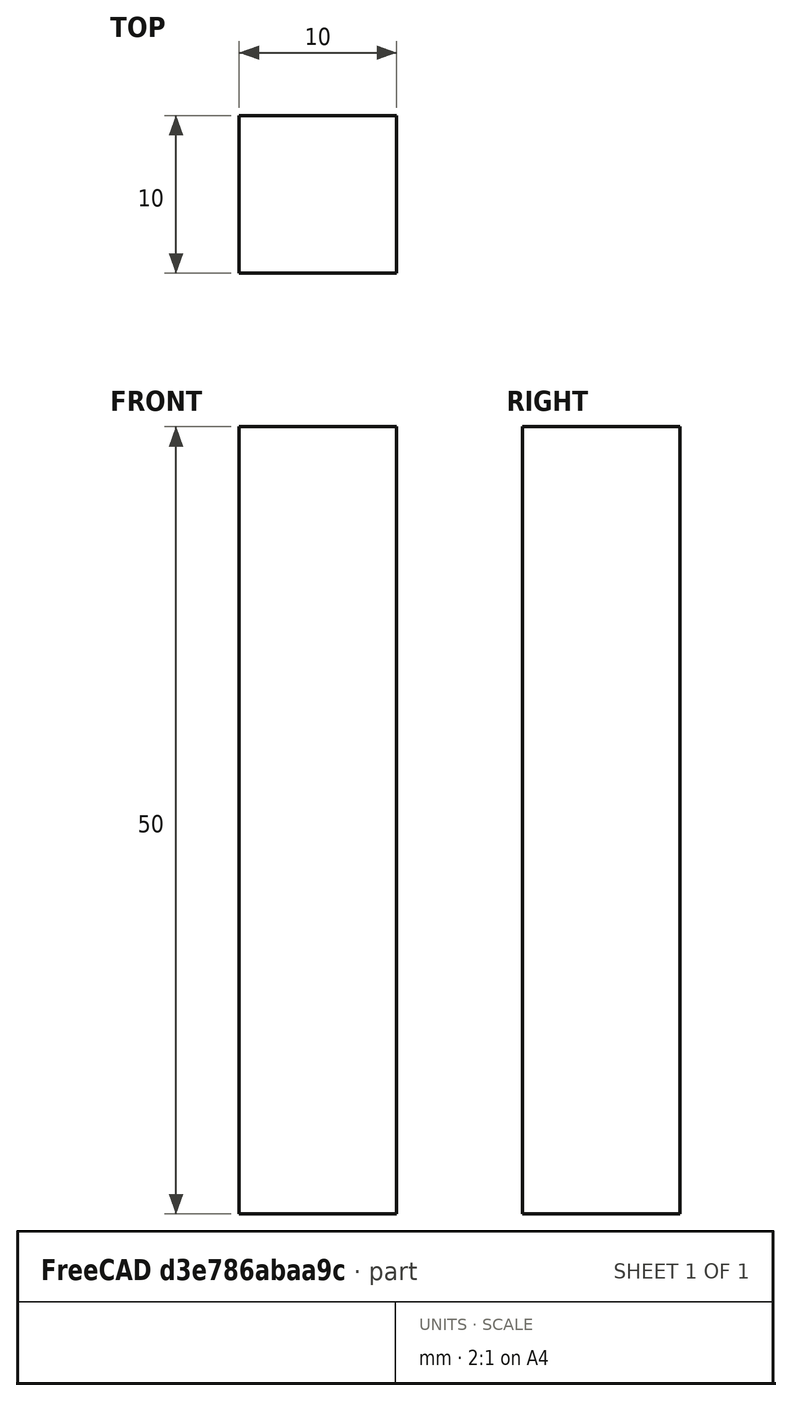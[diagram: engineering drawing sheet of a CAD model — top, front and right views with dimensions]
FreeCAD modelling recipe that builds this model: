
FCSTD DOCUMENT  (FreeCAD 0.15R4671 (Git))
Label: Square Bar 10 EN10059 S235JR
License: All rights reserved
LicenseURL: http://en.wikipedia.org/wiki/All_rights_reserved
objects: Sketcher::SketchObject×1, Part::Extrusion×1
note: 2 computed .brp shape members not serialized (recipe doc carries the construction recipe); baked Part::Feature solids carry a one-line shape summary decoded from their .brp

FEATURE [Sketcher::SketchObject] Sketch
  sketch-geometry (4):
    g0: LineSegment StartX=-5 StartY=-5 StartZ=0 EndX=5 EndY=-5 EndZ=0
    g1: LineSegment StartX=5 StartY=-5 StartZ=0 EndX=5 EndY=5 EndZ=0
    g2: LineSegment StartX=5 StartY=5 StartZ=0 EndX=-5 EndY=5 EndZ=0
    g3: LineSegment StartX=-5 StartY=5 StartZ=0 EndX=-5 EndY=-5 EndZ=0
  constraints (12):
    c: Coincident(g0,g1)
    c: Coincident(g1,g2)
    c: Coincident(g2,g3)
    c: Coincident(g3,g0)
    c: Horizontal(g0)
    c: Horizontal(g2)
    c: Vertical(g1)
    c: Vertical(g3)
    c: Symmetric(g1,g0,g-1)
    c: Symmetric(g2,g1,g-2)
    c: Equal(g1,g2)
    c: DistanceY(g1) = 10
FEATURE [Part::Extrusion] Extrude  label="Square Bar 10 EN10059 S235JR"
  Base = -> Sketch
  Dir = (0,0,50)
  Solid = true
